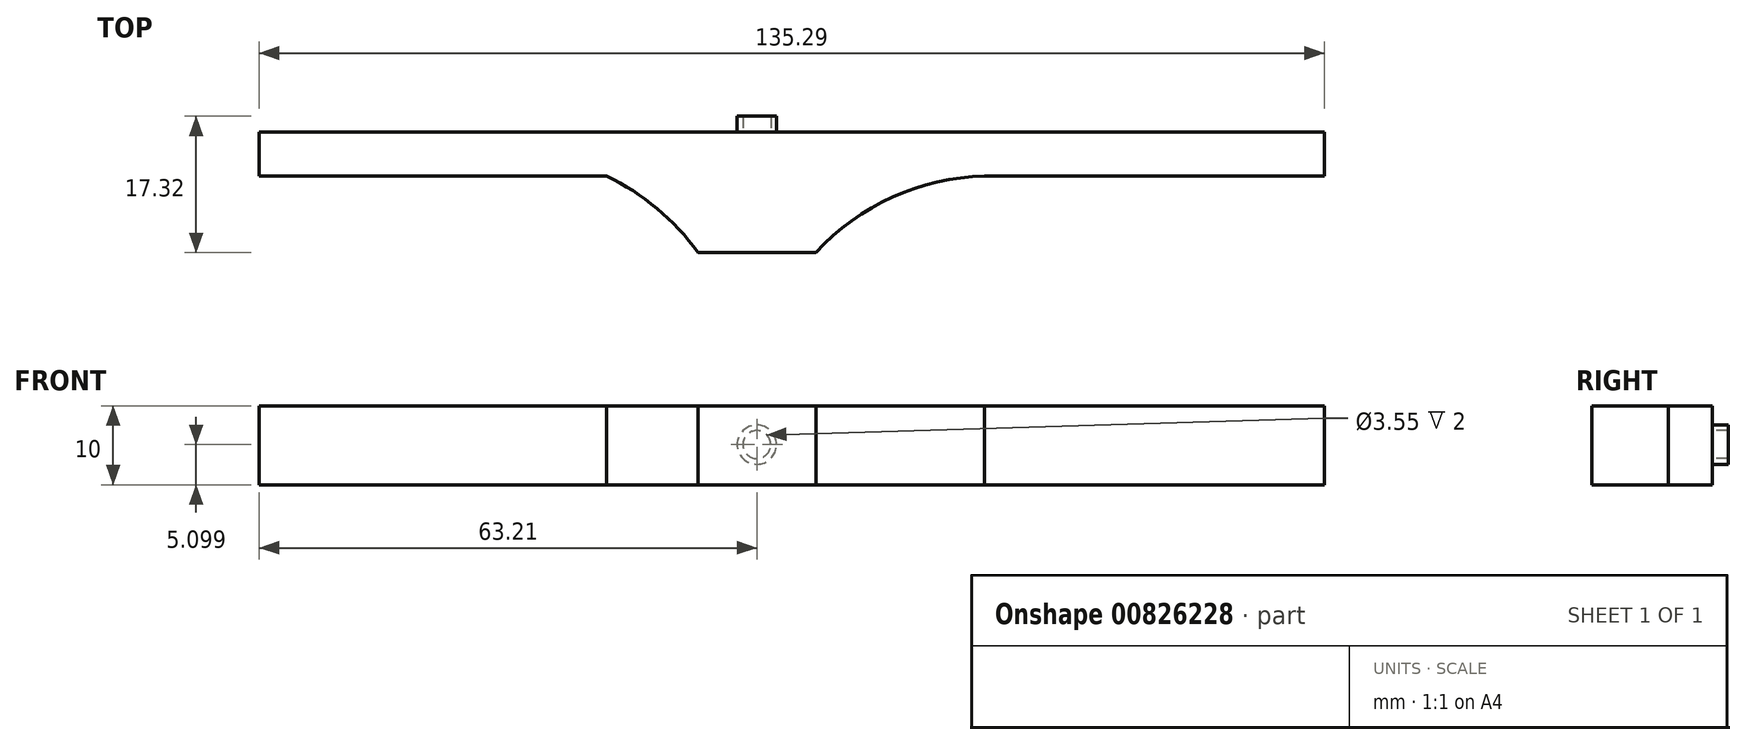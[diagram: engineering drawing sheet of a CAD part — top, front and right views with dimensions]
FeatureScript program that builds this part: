
annotation { "Feature Type Name" : "Feature", "Feature Type Description" : "" }
export const myFeature = defineFeature(function(context is Context, id is Id, definition is map)
    precondition{}
    {
        {
            var Q0;
            Q0=qCreatedBy(makeId("Top.planeOp"),FACE);
            var sketch = newSketch(context, id + "F0", { "sketchPlane" : qUnion([Q0])});
            skLineSegment(sketch, "E0", {"start": v(-7.5, -9.7) * mm, "end": v(7.5, -9.7) * mm});
            skArc(sketch, "E1", {"start": v(28.92, 0) * mm, "mid": v(17.22, -2.66) * mm, "end": v(7.5, -9.7) * mm});
            skArc(sketch, "E2", {"start": v(-7.5, -9.7) * mm, "mid": v(-12.67, -4.1) * mm, "end": v(-19.09, 0) * mm});
            skLineSegment(sketch, "E3", {"start": v(-19.09, 0) * mm, "end": v(-63.21, 0) * mm});
            skLineSegment(sketch, "E4", {"start": v(-63.21, 0) * mm, "end": v(-63.21, 5.62) * mm});
            skLineSegment(sketch, "E5", {"start": v(-63.21, 5.62) * mm, "end": v(72.08, 5.62) * mm});
            skLineSegment(sketch, "E6", {"start": v(72.08, 5.62) * mm, "end": v(72.08, 0) * mm});
            skLineSegment(sketch, "E7", {"start": v(72.08, 0) * mm, "end": v(28.92, 0) * mm});
            skSolve(sketch);
        }
        {
            var Q0;
            Q0 = qSketchRegion(id + "F0", true);
            extrude(context, id + "F1", {"entities" : qUnion([Q0]), "depth" : 10 * mm, "offsetDistance" : 25 * mm});
        }
        {
            var Q0;
            Q0=makeQuery(id+"F1.opExtrude","SWEPT_FACE",FACE,{"disambiguationData":[OSD([sQuery(id+"F0.wireOp",EDGE,"E5")])]});
            var sketch = newSketch(context, id + "F2", { "sketchPlane" : qUnion([Q0])});
            skCircle(sketch, "E8", {"center": v(0, 5.1) * mm, "radius": 2.5 * mm});
            skCircle(sketch, "E9.0", {"center": v(0, 5.1) * mm, "radius": 1.77 * mm});
            skSolve(sketch);
        }
        {
            var Q0;
            Q0 = qSketchRegion(id + "F2", true);
            extrude(context, id + "F3", {"entities" : qUnion([Q0]), "operationType" : NewBodyOperationType.ADD, "depth" : 2 * mm, "offsetDistance" : 25 * mm});
        }
    });
